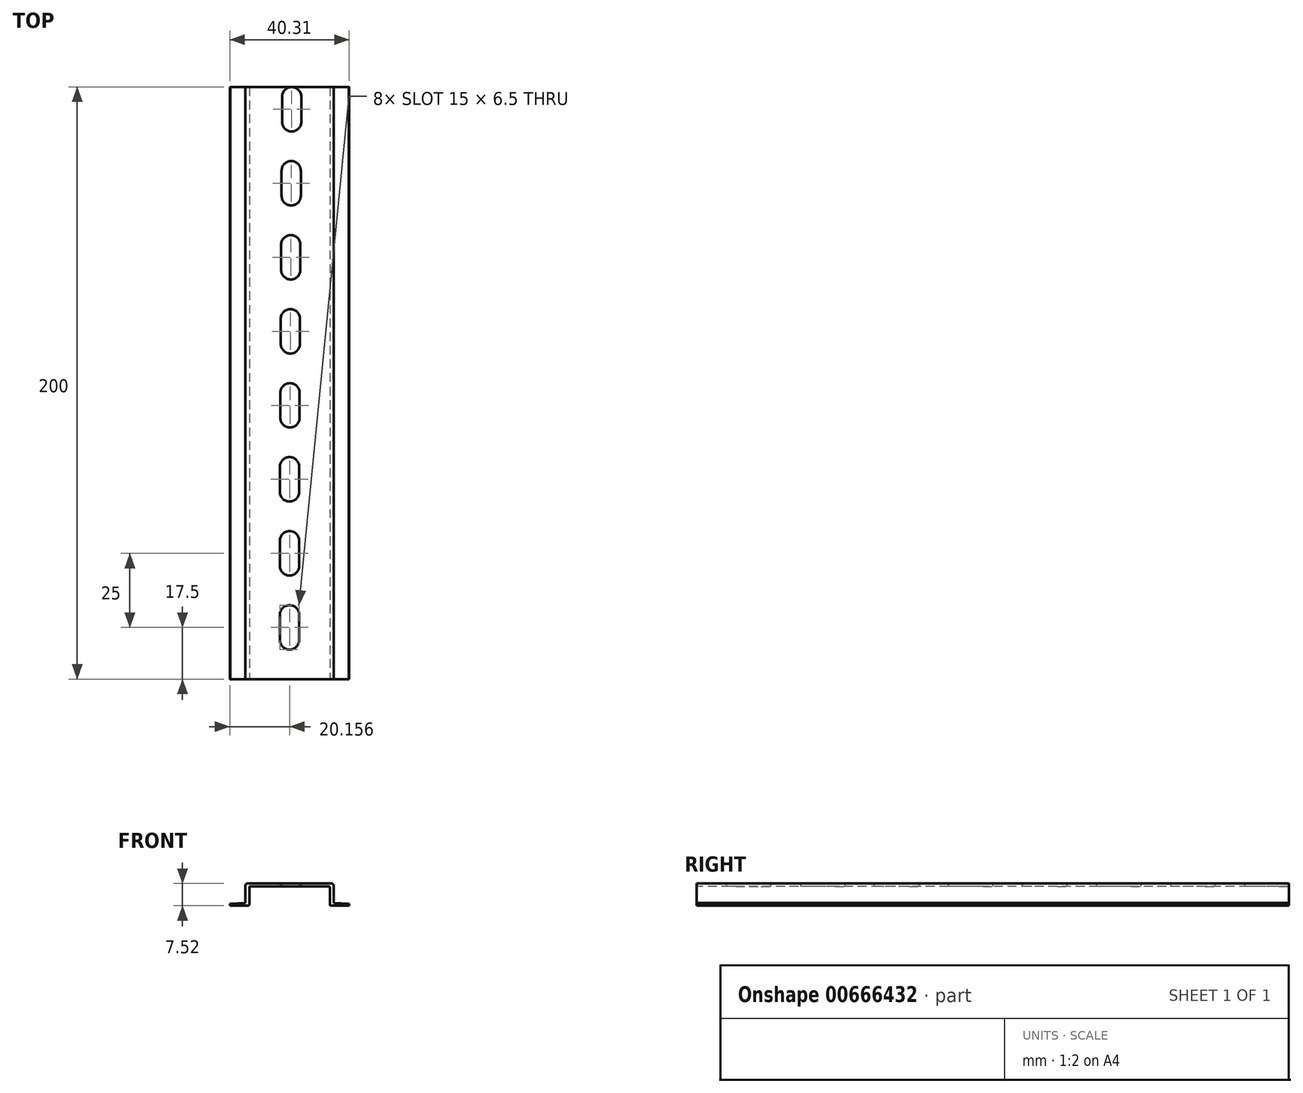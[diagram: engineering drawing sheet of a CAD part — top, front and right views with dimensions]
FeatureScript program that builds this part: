
annotation { "Feature Type Name" : "Feature", "Feature Type Description" : "" }
export const myFeature = defineFeature(function(context is Context, id is Id, definition is map)
    precondition{}
    {
        {
            var Q0;
            Q0=qCreatedBy(makeId("Front.planeOp"),FACE);
            var sketch = newSketch(context, id + "F0", { "sketchPlane" : qUnion([Q0])});
            skLineSegment(sketch, "E0.0", {"start": v(0, 1.23) * mm, "end": v(5.15, 1.49) * mm});
            skFitSpline(sketch, "E1.0.0", {"points": [v(40.07, 0.49) * mm, v(40.2, 0.86) * mm, v(40.07, 1.23) * mm]});
            skLineSegment(sketch, "E1.0.1", {"start": v(40.07, 1.23) * mm, "end": v(34.92, 1.49) * mm});
            skLineSegment(sketch, "E1.0.2", {"start": v(34.92, 1.49) * mm, "end": v(34.92, 7.31) * mm});
            skArc(sketch, "E1.0.3", {"start": v(34.92, 7.31) * mm, "mid": v(34.71, 7.8) * mm, "end": v(34.22, 8.01) * mm});
            skLineSegment(sketch, "E1.0.4", {"start": v(34.22, 8.01) * mm, "end": v(5.85, 8.01) * mm});
            skArc(sketch, "E1.0.5", {"start": v(5.85, 8.01) * mm, "mid": v(5.36, 7.8) * mm, "end": v(5.15, 7.31) * mm});
            skLineSegment(sketch, "E1.0.6", {"start": v(5.15, 7.31) * mm, "end": v(5.15, 1.49) * mm});
            skLineSegment(sketch, "E1.0.7", {"start": v(5.15, 1.49) * mm, "end": v(0, 1.23) * mm});
            skFitSpline(sketch, "E1.0.8", {"points": [v(0, 1.23) * mm, v(-0.12, 0.86) * mm, v(0, 0.49) * mm]});
            skLineSegment(sketch, "E1.0.9", {"start": v(0, 0.49) * mm, "end": v(5.95, 0.49) * mm});
            skArc(sketch, "E1.0.10", {"start": v(5.95, 0.49) * mm, "mid": v(6.3, 0.63) * mm, "end": v(6.45, 0.99) * mm});
            skLineSegment(sketch, "E1.0.11", {"start": v(6.45, 0.99) * mm, "end": v(6.45, 6.71) * mm});
            skArc(sketch, "E1.0.12", {"start": v(6.45, 6.71) * mm, "mid": v(6.54, 6.93) * mm, "end": v(6.75, 7.01) * mm});
            skLineSegment(sketch, "E1.0.13", {"start": v(6.75, 7.01) * mm, "end": v(33.32, 7.01) * mm});
            skArc(sketch, "E1.0.14", {"start": v(33.32, 7.01) * mm, "mid": v(33.53, 6.93) * mm, "end": v(33.62, 6.71) * mm});
            skLineSegment(sketch, "E1.0.15", {"start": v(33.62, 6.71) * mm, "end": v(33.62, 0.99) * mm});
            skArc(sketch, "E1.0.16", {"start": v(33.62, 0.99) * mm, "mid": v(33.77, 0.63) * mm, "end": v(34.12, 0.49) * mm});
            skLineSegment(sketch, "E1.0.17", {"start": v(34.12, 0.49) * mm, "end": v(40.07, 0.49) * mm});
            skSolve(sketch);
        }
        {
            var Q0;
            Q0 = qSketchRegion(id + "F0", true);
            extrude(context, id + "F1", {"entities" : qUnion([Q0]), "oppositeDirection" : true, "depth" : 200 * mm, "offsetDistance" : 25 * mm});
        }
        {
            var Q0;
            Q0=qCreatedBy(makeId("Top.planeOp"),FACE);
            var sketch = newSketch(context, id + "F2", { "sketchPlane" : qUnion([Q0])});
            skLineSegment(sketch, "E2.0", {"start": v(16.79, 21.75) * mm, "end": v(16.79, 13.25) * mm});
            skArc(sketch, "E3.0", {"start": v(23.29, 21.75) * mm, "mid": v(20.04, 25) * mm, "end": v(16.79, 21.75) * mm});
            skLineSegment(sketch, "E4.0", {"start": v(23.29, 13.25) * mm, "end": v(23.29, 21.75) * mm});
            skArc(sketch, "E5.0", {"start": v(16.79, 13.25) * mm, "mid": v(20.04, 10) * mm, "end": v(23.29, 13.25) * mm});
            skArc(sketch, "E6.0", {"start": v(16.79, 38.25) * mm, "mid": v(20.04, 35) * mm, "end": v(23.29, 38.25) * mm});
            skArc(sketch, "E7.0", {"start": v(23.29, 46.75) * mm, "mid": v(20.04, 50) * mm, "end": v(16.79, 46.75) * mm});
            skLineSegment(sketch, "E8.0", {"start": v(23.29, 38.25) * mm, "end": v(23.29, 46.75) * mm});
            skLineSegment(sketch, "E9.0", {"start": v(23.29, 63.25) * mm, "end": v(23.29, 71.75) * mm});
            skArc(sketch, "E10.0", {"start": v(23.29, 71.75) * mm, "mid": v(20.04, 75) * mm, "end": v(16.79, 71.75) * mm});
            skLineSegment(sketch, "E11.0", {"start": v(16.79, 71.75) * mm, "end": v(16.79, 63.25) * mm});
            skArc(sketch, "E12.0", {"start": v(16.79, 63.25) * mm, "mid": v(20.04, 60) * mm, "end": v(23.29, 63.25) * mm});
            skLineSegment(sketch, "E13", {"start": v(16.79, 46.75) * mm, "end": v(16.79, 38.25) * mm});
            skLineSegment(sketch, "E14.1.0.0", {"start": v(23.43, 88.25) * mm, "end": v(23.43, 96.75) * mm});
            skArc(sketch, "E14.1.0.1", {"start": v(16.93, 88.25) * mm, "mid": v(20.18, 85) * mm, "end": v(23.43, 88.25) * mm});
            skLineSegment(sketch, "E14.1.0.2", {"start": v(16.93, 96.75) * mm, "end": v(16.93, 88.25) * mm});
            skArc(sketch, "E14.1.0.3", {"start": v(23.43, 96.75) * mm, "mid": v(20.18, 100) * mm, "end": v(16.93, 96.75) * mm});
            skLineSegment(sketch, "E14.2.0.0", {"start": v(23.57, 113.25) * mm, "end": v(23.57, 121.75) * mm});
            skArc(sketch, "E14.2.0.1", {"start": v(17.07, 113.25) * mm, "mid": v(20.32, 110) * mm, "end": v(23.57, 113.25) * mm});
            skLineSegment(sketch, "E14.2.0.2", {"start": v(17.07, 121.75) * mm, "end": v(17.07, 113.25) * mm});
            skArc(sketch, "E14.2.0.3", {"start": v(23.57, 121.75) * mm, "mid": v(20.32, 125) * mm, "end": v(17.07, 121.75) * mm});
            skLineSegment(sketch, "E14.3.0.0", {"start": v(23.7, 138.25) * mm, "end": v(23.7, 146.75) * mm});
            skArc(sketch, "E14.3.0.1", {"start": v(17.2, 138.25) * mm, "mid": v(20.46, 135) * mm, "end": v(23.7, 138.25) * mm});
            skLineSegment(sketch, "E14.3.0.2", {"start": v(17.2, 146.75) * mm, "end": v(17.2, 138.25) * mm});
            skArc(sketch, "E14.3.0.3", {"start": v(23.7, 146.75) * mm, "mid": v(20.46, 150) * mm, "end": v(17.2, 146.75) * mm});
            skLineSegment(sketch, "E14.4.0.0", {"start": v(23.85, 163.25) * mm, "end": v(23.85, 171.75) * mm});
            skArc(sketch, "E14.4.0.1", {"start": v(17.35, 163.25) * mm, "mid": v(20.6, 160) * mm, "end": v(23.85, 163.25) * mm});
            skLineSegment(sketch, "E14.4.0.2", {"start": v(17.35, 171.75) * mm, "end": v(17.35, 163.25) * mm});
            skArc(sketch, "E14.4.0.3", {"start": v(23.85, 171.75) * mm, "mid": v(20.6, 175) * mm, "end": v(17.35, 171.75) * mm});
            skLineSegment(sketch, "E14.5.0.0", {"start": v(24, 188.25) * mm, "end": v(24, 196.75) * mm});
            skArc(sketch, "E14.5.0.1", {"start": v(17.5, 188.25) * mm, "mid": v(20.74, 185) * mm, "end": v(24, 188.25) * mm});
            skLineSegment(sketch, "E14.5.0.2", {"start": v(17.5, 196.75) * mm, "end": v(17.5, 188.25) * mm});
            skArc(sketch, "E14.5.0.3", {"start": v(24, 196.75) * mm, "mid": v(20.74, 200) * mm, "end": v(17.5, 196.75) * mm});
            skLineSegment(sketch, "E14.direction1", {"start": v(16.79, 63.25) * mm, "end": v(16.93, 88.25) * mm, "construction": true});
            skSolve(sketch);
        }
        {
            var Q0;
            Q0 = qSketchRegion(id + "F2", true);
            extrude(context, id + "F3", {"entities" : qUnion([Q0]), "operationType" : NewBodyOperationType.REMOVE, "endBound" : BoundingType.THROUGH_ALL, "depth" : 25 * mm, "offsetDistance" : 25 * mm});
        }
    });
